# Revit family: Fantom_Eng
name_source: partatom
category: Mechanical Equipment
units: mm (PartAtom-declared; Revit-internal decimal feet)

## family parameters
Always vertical = Yes
Classification = None
Cut with Voids When Loaded = No
Part Type = Normal
Room Calculation Point = No
Round Connector Dimension = Use Diameter
Shared = No
Work Plane-Based = No

## types (1)
- Fantom
    00_20_Manufacturer = Vents
    00_20_Name = Centrifugal fan
    00_20_Type = Fantom
    Amperage = 0.116 A
    B = 215 mm  [stored 0.705381 ft]
    B1 = 115 mm  [stored 0.377297 ft]
    Casing Material = Plastic, opaque, white
    D = 100 mm  [stored 0.328084 ft]
    Default Elevation = 0 mm  [stored 0 ft]
    Diameter = 100 mm  [stored 0.328084 ft]
    Dy = 95 mm
    Frequency = 50 Hz
    H = 256 mm  [stored 0.839895 ft]
    H1 = 156 mm  [stored 0.511811 ft]
    Height = 256 mm  [stored 0.839895 ft]
    L = 115 mm  [stored 0.377297 ft]
    L1 = 37 mm  [stored 0.121391 ft]
    Length = 115 mm  [stored 0.377297 ft]
    Load Classification = HVAC
    Maintenance zone material = <By Category>
    Manufacturer = Vents
    Maximum Air Flow = 107.0 m³/h
    Number of Fase = 1
    Power = 27 W
    Sound pressure level at 3 m distance = 35.5 dBA
    Voltage = 230 V
    Width = 215 mm  [stored 0.705381 ft]

note: [stored X ft] marks values corroborated as IEEE doubles in the binary element streams (Revit-internal decimal feet)
